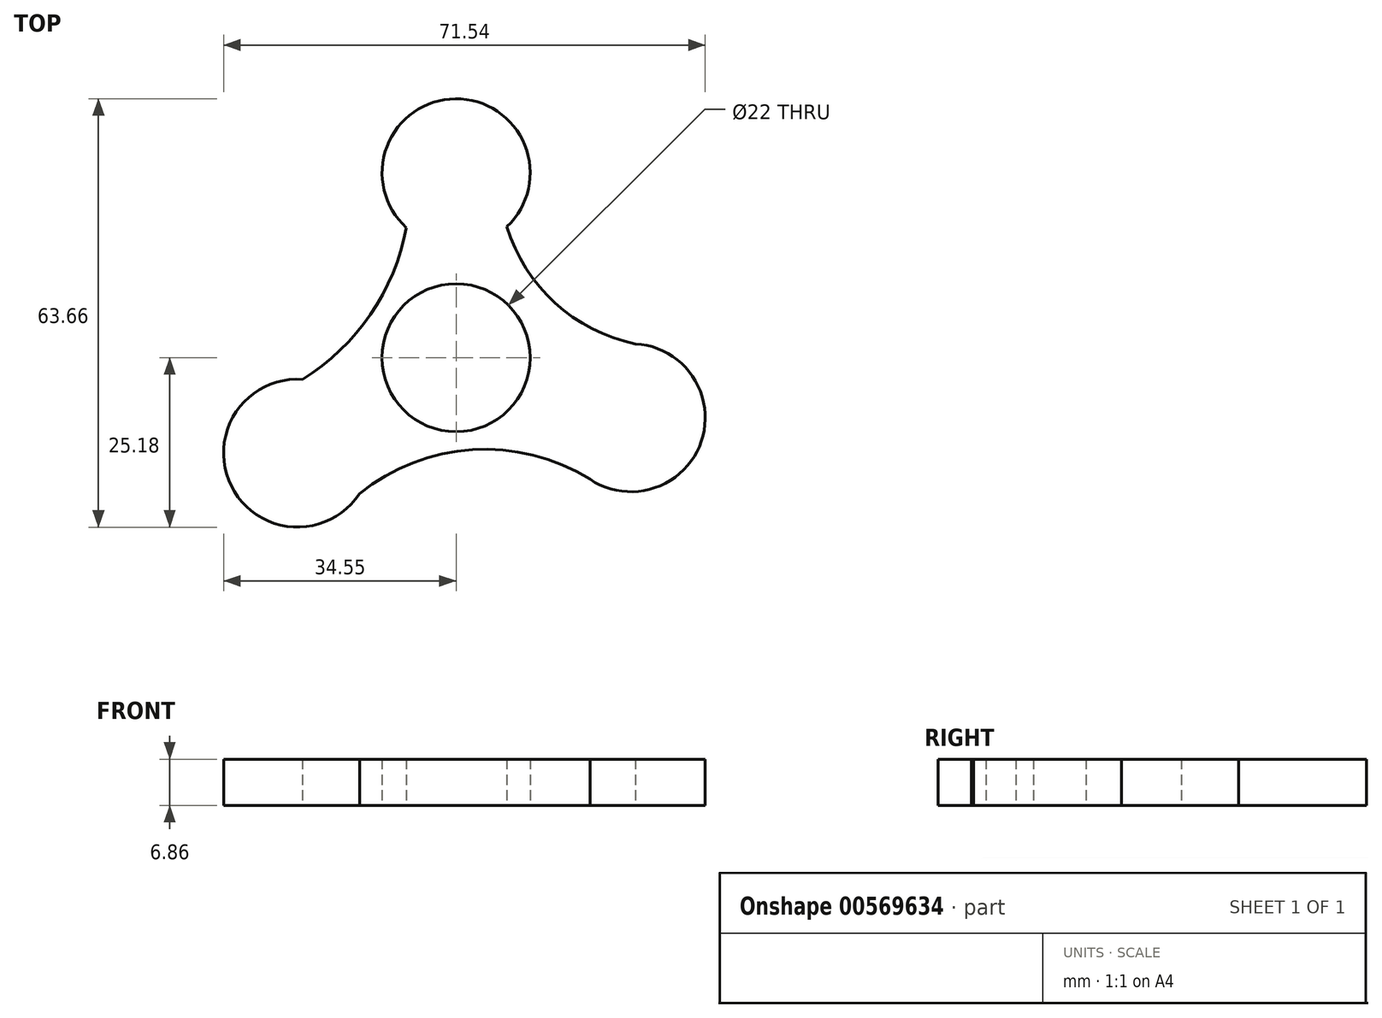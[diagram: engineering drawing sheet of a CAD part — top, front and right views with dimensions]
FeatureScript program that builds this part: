
annotation { "Feature Type Name" : "Feature", "Feature Type Description" : "" }
export const myFeature = defineFeature(function(context is Context, id is Id, definition is map)
    precondition{}
    {
        {
            var Q0;
            Q0=qCreatedBy(makeId("Top.planeOp"),FACE);
            var sketch = newSketch(context, id + "F0", { "sketchPlane" : qUnion([Q0])});
            skCircle(sketch, "E0", {"center": v(0, 0) * mm, "radius": 11 * mm});
            skCircle(sketch, "E1", {"center": v(26, -8.92) * mm, "radius": 11 * mm});
            skCircle(sketch, "E2", {"center": v(-23.55, -14.19) * mm, "radius": 11 * mm});
            skCircle(sketch, "E3", {"center": v(0, 27.48) * mm, "radius": 11 * mm});
            skArc(sketch, "E4", {"start": v(-22.8, -3.21) * mm, "mid": v(-12.72, 6.43) * mm, "end": v(-7.38, 19.33) * mm});
            skArc(sketch, "E5", {"start": v(7.54, 19.48) * mm, "mid": v(14.7, 8.15) * mm, "end": v(26.64, 2.06) * mm});
            skArc(sketch, "E6", {"start": v(19.9, -18.07) * mm, "mid": v(2.42, -13.68) * mm, "end": v(-14.36, -20.22) * mm});
            skSolve(sketch);
        }
        {
            var Q0;
            Q0 = qSketchRegion(id + "F0", true);
            extrude(context, id + "F1", {"entities" : qUnion([Q0]), "depth" : 6.86 * mm, "offsetDistance" : 25.4 * mm});
        }
    });
